# Revit family: EN 160 ATJ STV
name_source: partatom
category: Equipement spécialisé
units: mm (PartAtom-declared; Revit-internal decimal feet)

## family parameters
Basée sur le plan de construction = Non
Cote de connecteur circulaire = Utiliser le diamètre
Couper avec des vides une fois chargée = Non
Numéro OmniClass = 23.50.00.00
Partagée = Non
Point de calcul de pièce = Non
Titre OmniClass = Conveying Systems & Material Handling
Toujours verticalement = Oui
Type d'élément = Normal

## types (1)
- 160 ATJ STV
    Average consumption (L/h) = 1.226
    Average consumption (l/day) = 0 m
    CO2 emissions (g/kWh) = 3.2
    Commentaires du type = Nacelle élévatrice Diesel de 16m de hauteur de travail
    Counterweight offset (turret at 90°) = 0.22 m
    Créé par = ATLANCAD
    Elévation par défaut = 0 m
    Engine norm = STAGE V
    External turning radius = 3.75 m
    Fabricant = MANITOU
    Floor height (access) = 0.4 m
    Ground clearance = 0.26 m
    Ground clearance at centre of wheelbase = 0.36 m
    I.C. Engine power rating - Power (ch) = 24.5
    I.C. Engine power rating - Power (kW) = 18.5
    Internal turning radius (over tyres) = 1.39 m
    Jib length = 1.7 m
    Max. lifting height = 16.02 m
    Max. outreach = 8.3 m
    Modèle = 160 ATJ STV
    Noise to environment (LwA) = 105
    Number of people (inside) = 2
    Number of people (outside) = 2
    Overall height (stowed) = 2.63 m
    Overall height (transport) = 2.37 m
    Overall lenght (stowed) = 4.44 m
    Overall lenght (transport) = 6.68 m
    Overhang = 0 m
    Permissible leveling = 5.00°
    Platform capacity = 230.00 kg
    Platform dimensions (length) = 1.8 m
    Platform dimensions (width) = 0.8 m
    Platform weight = 6118.00 kg
    URL = www.manitou.com
    Wheelbase = 2.2 m
    Width = 2.32 m
